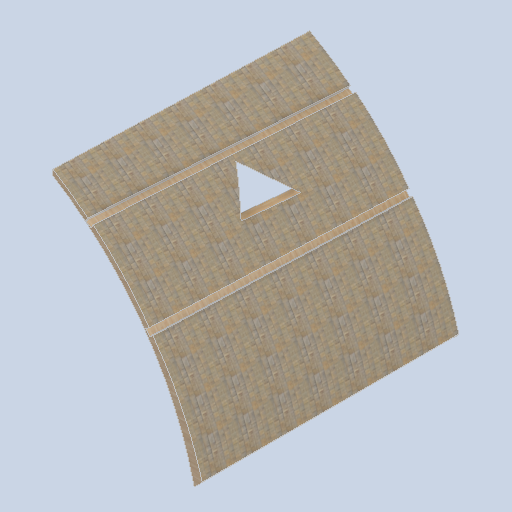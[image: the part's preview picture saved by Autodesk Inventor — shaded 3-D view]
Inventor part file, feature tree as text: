
AUTODESK INVENTOR PART (.ipt)
format: ipt  version: 2024.2 (Build 282272000, 272)  size: 371,200 bytes
history: native  units: in
note: dims shown in document units (in); Inventor stores cm internally (conversion verified against a paired STEP export)
features: other x3, sketch x2, plane x2
ambient origin geometry x8: Origin, YZ Plane, XZ Plane, XY Plane, X Axis, Y Axis, Z Axis, Center Point
bodies: Solid1 (feature_tree)
feature tree (7):
  other  "panel_block_03.ipt"
  other  "Solid1::panel_block_03.ipt"
  other  "TaggingFeature1"
  sketch  "Sketch1"  dims[d0=0.3937in]
  sketch  "Sketch2"
  plane  "Work Plane1"
  plane  "Work Plane2"
